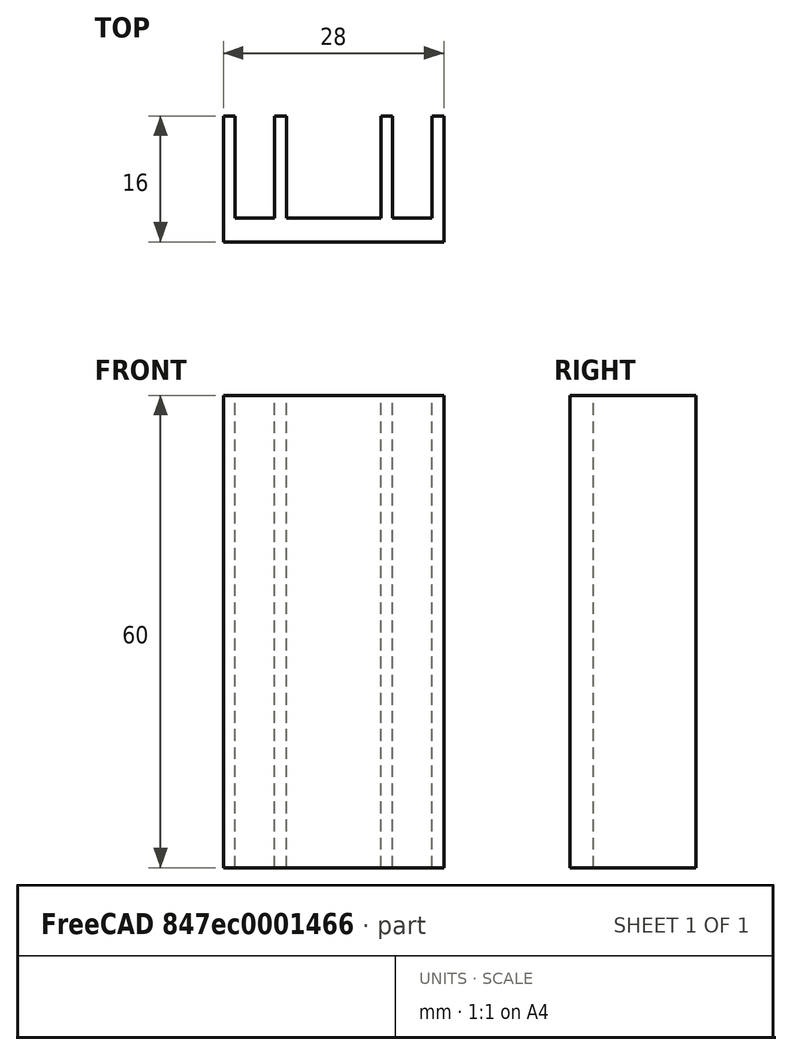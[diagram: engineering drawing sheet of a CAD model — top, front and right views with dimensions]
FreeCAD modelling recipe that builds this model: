
FCSTD DOCUMENT  (FreeCAD 0.21R33694 (Git))
Label: teste
License: All rights reserved
LicenseURL: https://en.wikipedia.org/wiki/All_rights_reserved
objects: Part::Part2DObjectPython×1, Part::Extrusion×1
note: 2 computed .brp shape members not serialized (recipe doc carries the construction recipe); baked Part::Feature solids carry a one-line shape summary decoded from their .brp

FEATURE [Part::Part2DObjectPython] Wire  # Draft 2D object (typed FeaturePython)
  Area = 0
  ChamferSize = 0
  Closed = false
  End = (6.43109,1.6592,2.197e-13)
  FilletRadius = 0
  Length = 166
  MakeFace = true
  Placement = pos=(6.43109,1.6592,2.197e-13) rot=(0,0,1;1e-06rad)
  Points = (17) [(0,0,0),(28,0,-2.01948e-28),(28,16,-2.01948e-28),(26.5,16,0),(26.5,3,0),(21.5,3,0),(21.5,16,2.01948e-28),(20,16,2.01948e-28),(20,3,2.01948e-28),+8 more]
  Start = (6.43109,1.6592,2.197e-13)
  Subdivisions = 0
FEATURE [Part::Extrusion] Extrude
  Base = -> Wire
  Dir = (-2.96e-14,-1.75e-14,1)
  DirMode = 2
  FaceMakerClass = Part::FaceMakerBullseye
  LengthFwd = 60
  LengthRev = 0
  Solid = true
  Symmetric = false
